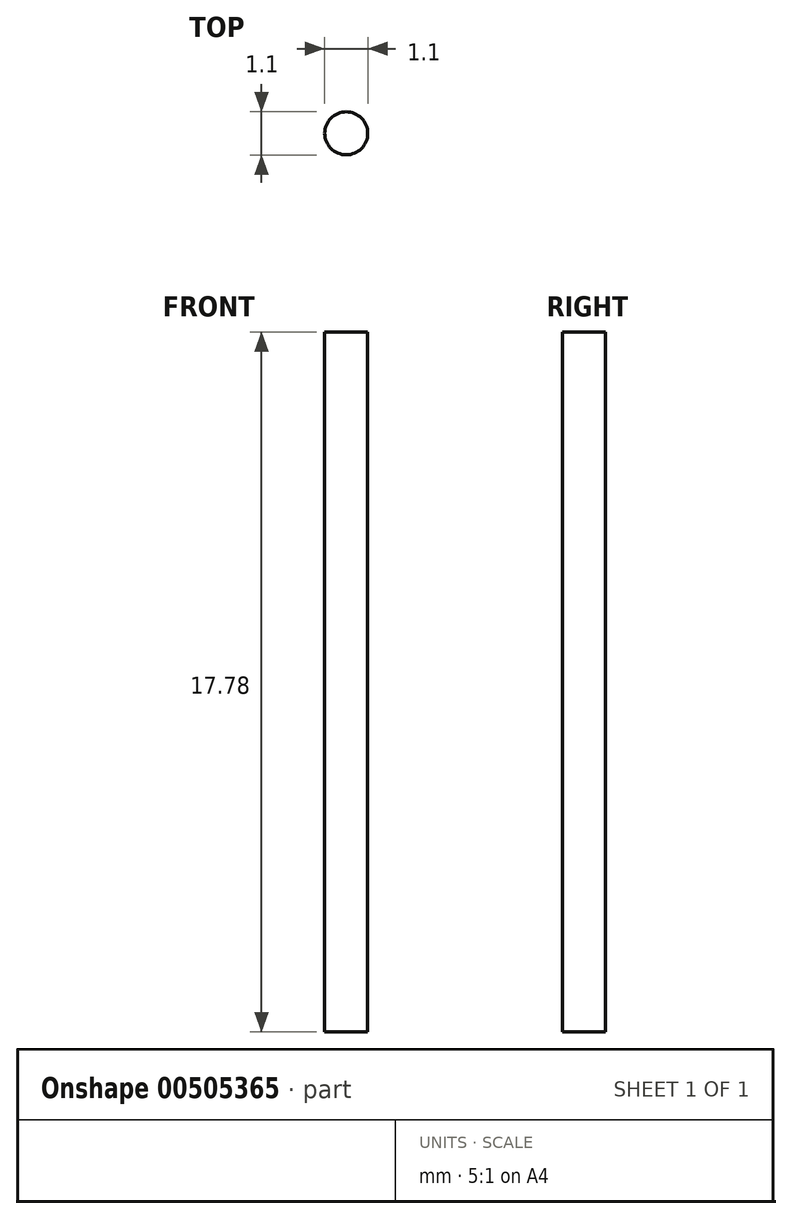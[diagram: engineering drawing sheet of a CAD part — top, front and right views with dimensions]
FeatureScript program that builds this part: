
annotation { "Feature Type Name" : "Feature", "Feature Type Description" : "" }
export const myFeature = defineFeature(function(context is Context, id is Id, definition is map)
    precondition{}
    {
        {
            var Q0;
            Q0=qCreatedBy(makeId("Top.planeOp"),FACE);
            var sketch = newSketch(context, id + "F0", { "sketchPlane" : qUnion([Q0])});
            skCircle(sketch, "E0", {"center": v(0, 25.4) * mm, "radius": 0.55 * mm});
            skSolve(sketch);
        }
        {
            var Q0;
            Q0 = qSketchRegion(id + "F0", true);
            extrude(context, id + "F1", {"entities" : qUnion([Q0]), "depth" : 17.78 * mm});
        }
    });
